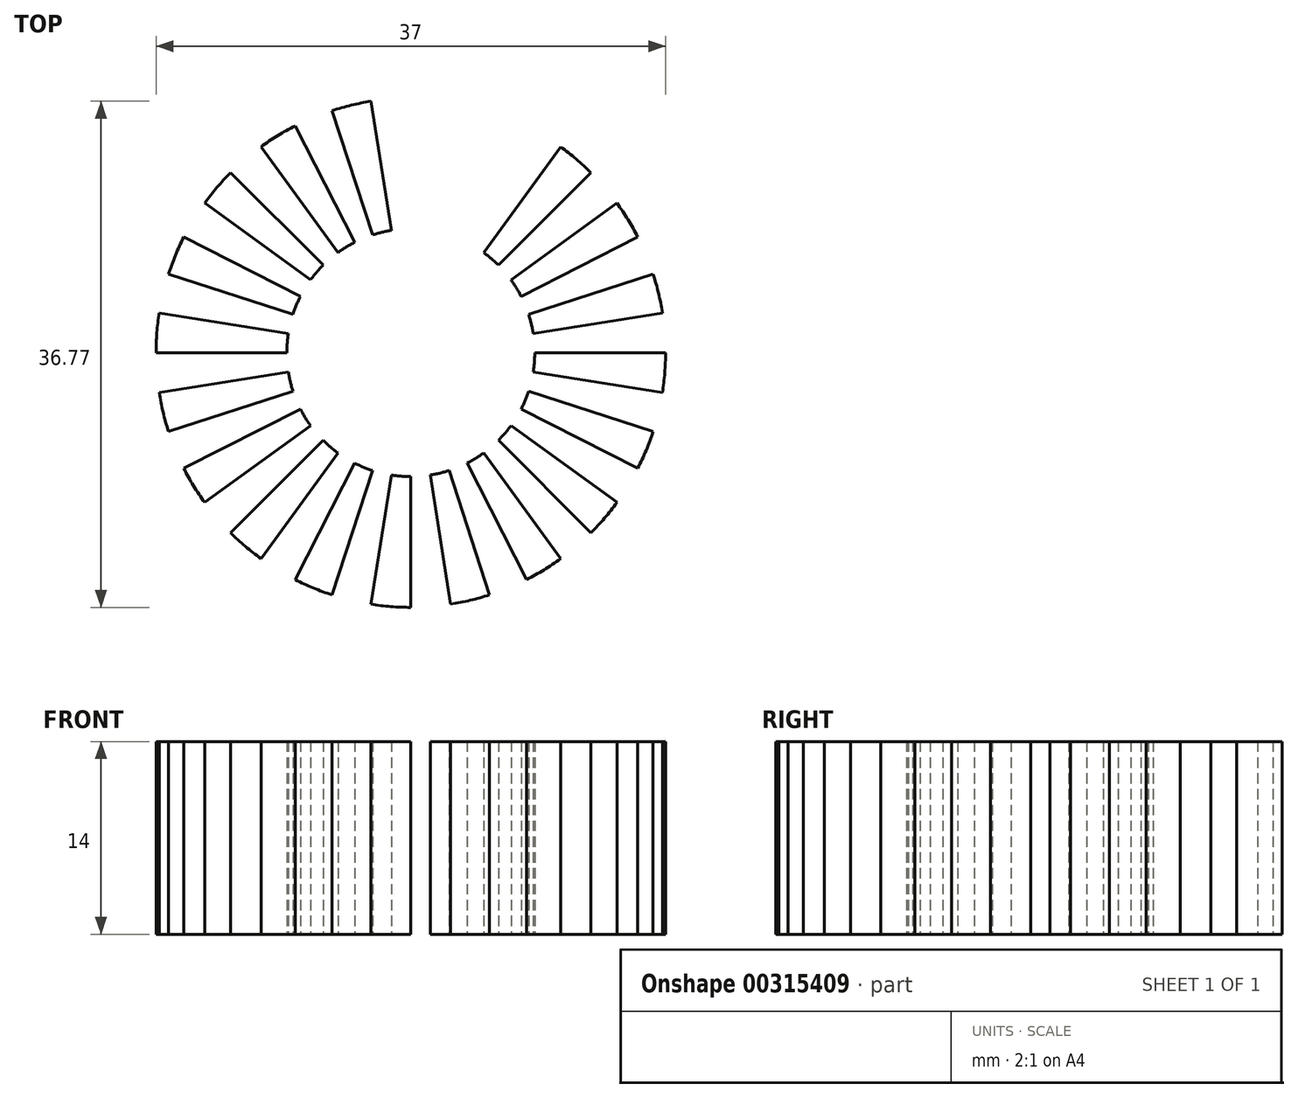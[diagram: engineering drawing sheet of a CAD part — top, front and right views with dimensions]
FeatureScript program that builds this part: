
annotation { "Feature Type Name" : "Feature", "Feature Type Description" : "" }
export const myFeature = defineFeature(function(context is Context, id is Id, definition is map)
    precondition{}
    {
        {
            var Q0;
            Q0=qCreatedBy(makeId("Top.planeOp"),FACE);
            var sketch = newSketch(context, id + "F0", { "sketchPlane" : qUnion([Q0])});
            skCircle(sketch, "E0", {"center": v(0, 0) * mm, "radius": 18.5 * mm, "construction": true});
            skArc(sketch, "E1", {"start": v(0, 18.5) * mm, "mid": v(1.45, 18.44) * mm, "end": v(2.9, 18.27) * mm});
            skLineSegment(sketch, "E2", {"start": v(2.9, 18.27) * mm, "end": v(1.4, 8.89) * mm});
            skArc(sketch, "E3", {"start": v(2.66, 16.8) * mm, "mid": v(3.97, 16.53) * mm, "end": v(5.25, 16.17) * mm});
            skLineSegment(sketch, "E4", {"start": v(5.25, 16.17) * mm, "end": v(2.78, 8.56) * mm});
            skLineSegment(sketch, "E5", {"start": v(0, 18.5) * mm, "end": v(0, 9) * mm});
            skArc(sketch, "E6", {"start": v(2.78, 8.56) * mm, "mid": v(1.4, 8.89) * mm, "end": v(0, 9) * mm});
            skLineSegment(sketch, "E7.1.0", {"start": v(-5.72, 17.6) * mm, "end": v(-2.78, 8.56) * mm});
            skArc(sketch, "E7.1.1", {"start": v(0, 9) * mm, "mid": v(-1.4, 8.89) * mm, "end": v(-2.78, 8.56) * mm});
            skLineSegment(sketch, "E7.1.2", {"start": v(0, 17) * mm, "end": v(0, 9) * mm});
            skArc(sketch, "E7.1.3", {"start": v(-2.66, 16.8) * mm, "mid": v(-1.33, 16.95) * mm, "end": v(0, 17) * mm});
            skLineSegment(sketch, "E7.1.4", {"start": v(-2.9, 18.27) * mm, "end": v(-1.4, 8.89) * mm});
            skArc(sketch, "E7.1.5", {"start": v(-5.72, 17.6) * mm, "mid": v(-4.32, 17.99) * mm, "end": v(-2.9, 18.27) * mm});
            skLineSegment(sketch, "E7.2.0", {"start": v(-10.87, 14.97) * mm, "end": v(-5.3, 7.28) * mm});
            skArc(sketch, "E7.2.1", {"start": v(-2.78, 8.56) * mm, "mid": v(-4.09, 8.02) * mm, "end": v(-5.3, 7.28) * mm});
            skLineSegment(sketch, "E7.2.2", {"start": v(-5.25, 16.17) * mm, "end": v(-2.78, 8.56) * mm});
            skArc(sketch, "E7.2.3", {"start": v(-7.72, 15.15) * mm, "mid": v(-6.5, 15.7) * mm, "end": v(-5.25, 16.17) * mm});
            skLineSegment(sketch, "E7.2.4", {"start": v(-8.4, 16.48) * mm, "end": v(-4.09, 8.02) * mm});
            skArc(sketch, "E7.2.5", {"start": v(-10.87, 14.97) * mm, "mid": v(-9.67, 15.77) * mm, "end": v(-8.4, 16.48) * mm});
            skLineSegment(sketch, "E7.3.0", {"start": v(-14.97, 10.87) * mm, "end": v(-7.28, 5.3) * mm});
            skArc(sketch, "E7.3.1", {"start": v(-5.3, 7.28) * mm, "mid": v(-6.36, 6.36) * mm, "end": v(-7.28, 5.3) * mm});
            skLineSegment(sketch, "E7.3.2", {"start": v(-10, 13.75) * mm, "end": v(-5.3, 7.28) * mm});
            skArc(sketch, "E7.3.3", {"start": v(-12.02, 12.02) * mm, "mid": v(-11.04, 12.93) * mm, "end": v(-10, 13.75) * mm});
            skLineSegment(sketch, "E7.3.4", {"start": v(-13.08, 13.08) * mm, "end": v(-6.36, 6.36) * mm});
            skArc(sketch, "E7.3.5", {"start": v(-14.97, 10.87) * mm, "mid": v(-14.07, 12.01) * mm, "end": v(-13.08, 13.08) * mm});
            skLineSegment(sketch, "E7.4.0", {"start": v(-17.6, 5.72) * mm, "end": v(-8.56, 2.78) * mm});
            skArc(sketch, "E7.4.1", {"start": v(-7.28, 5.3) * mm, "mid": v(-8.02, 4.09) * mm, "end": v(-8.56, 2.78) * mm});
            skLineSegment(sketch, "E7.4.2", {"start": v(-13.75, 10) * mm, "end": v(-7.28, 5.3) * mm});
            skArc(sketch, "E7.4.3", {"start": v(-15.15, 7.72) * mm, "mid": v(-14.5, 8.88) * mm, "end": v(-13.75, 10) * mm});
            skLineSegment(sketch, "E7.4.4", {"start": v(-16.48, 8.4) * mm, "end": v(-8.02, 4.09) * mm});
            skArc(sketch, "E7.4.5", {"start": v(-17.6, 5.72) * mm, "mid": v(-17.1, 7.08) * mm, "end": v(-16.48, 8.4) * mm});
            skLineSegment(sketch, "E7.5.0", {"start": v(-18.5, 0) * mm, "end": v(-9, 0) * mm});
            skArc(sketch, "E7.5.1", {"start": v(-8.56, 2.78) * mm, "mid": v(-8.89, 1.4) * mm, "end": v(-9, 0) * mm});
            skLineSegment(sketch, "E7.5.2", {"start": v(-16.17, 5.25) * mm, "end": v(-8.56, 2.78) * mm});
            skArc(sketch, "E7.5.3", {"start": v(-16.8, 2.66) * mm, "mid": v(-16.53, 3.97) * mm, "end": v(-16.17, 5.25) * mm});
            skLineSegment(sketch, "E7.5.4", {"start": v(-18.27, 2.9) * mm, "end": v(-8.89, 1.4) * mm});
            skArc(sketch, "E7.5.5", {"start": v(-18.5, 0) * mm, "mid": v(-18.44, 1.45) * mm, "end": v(-18.27, 2.9) * mm});
            skLineSegment(sketch, "E7.6.0", {"start": v(-17.6, -5.72) * mm, "end": v(-8.56, -2.78) * mm});
            skArc(sketch, "E7.6.1", {"start": v(-9, 0) * mm, "mid": v(-8.89, -1.4) * mm, "end": v(-8.56, -2.78) * mm});
            skLineSegment(sketch, "E7.6.2", {"start": v(-17, 0) * mm, "end": v(-9, 0) * mm});
            skArc(sketch, "E7.6.3", {"start": v(-16.8, -2.66) * mm, "mid": v(-16.95, -1.33) * mm, "end": v(-17, 0) * mm});
            skLineSegment(sketch, "E7.6.4", {"start": v(-18.27, -2.9) * mm, "end": v(-8.89, -1.4) * mm});
            skArc(sketch, "E7.6.5", {"start": v(-17.6, -5.72) * mm, "mid": v(-17.99, -4.32) * mm, "end": v(-18.27, -2.9) * mm});
            skLineSegment(sketch, "E7.7.0", {"start": v(-14.97, -10.87) * mm, "end": v(-7.28, -5.3) * mm});
            skArc(sketch, "E7.7.1", {"start": v(-8.56, -2.78) * mm, "mid": v(-8.02, -4.09) * mm, "end": v(-7.28, -5.3) * mm});
            skLineSegment(sketch, "E7.7.2", {"start": v(-16.17, -5.25) * mm, "end": v(-8.56, -2.78) * mm});
            skArc(sketch, "E7.7.3", {"start": v(-15.15, -7.72) * mm, "mid": v(-15.7, -6.5) * mm, "end": v(-16.17, -5.25) * mm});
            skLineSegment(sketch, "E7.7.4", {"start": v(-16.48, -8.4) * mm, "end": v(-8.02, -4.09) * mm});
            skArc(sketch, "E7.7.5", {"start": v(-14.97, -10.87) * mm, "mid": v(-15.77, -9.67) * mm, "end": v(-16.48, -8.4) * mm});
            skLineSegment(sketch, "E7.8.0", {"start": v(-10.87, -14.97) * mm, "end": v(-5.3, -7.28) * mm});
            skArc(sketch, "E7.8.1", {"start": v(-7.28, -5.3) * mm, "mid": v(-6.36, -6.36) * mm, "end": v(-5.3, -7.28) * mm});
            skLineSegment(sketch, "E7.8.2", {"start": v(-13.75, -10) * mm, "end": v(-7.28, -5.3) * mm});
            skArc(sketch, "E7.8.3", {"start": v(-12.02, -12.02) * mm, "mid": v(-12.93, -11.04) * mm, "end": v(-13.75, -10) * mm});
            skLineSegment(sketch, "E7.8.4", {"start": v(-13.08, -13.08) * mm, "end": v(-6.36, -6.36) * mm});
            skArc(sketch, "E7.8.5", {"start": v(-10.87, -14.97) * mm, "mid": v(-12.01, -14.07) * mm, "end": v(-13.08, -13.08) * mm});
            skLineSegment(sketch, "E7.9.0", {"start": v(-5.72, -17.6) * mm, "end": v(-2.78, -8.56) * mm});
            skArc(sketch, "E7.9.1", {"start": v(-5.3, -7.28) * mm, "mid": v(-4.09, -8.02) * mm, "end": v(-2.78, -8.56) * mm});
            skLineSegment(sketch, "E7.9.2", {"start": v(-10, -13.75) * mm, "end": v(-5.3, -7.28) * mm});
            skArc(sketch, "E7.9.3", {"start": v(-7.72, -15.15) * mm, "mid": v(-8.88, -14.5) * mm, "end": v(-10, -13.75) * mm});
            skLineSegment(sketch, "E7.9.4", {"start": v(-8.4, -16.48) * mm, "end": v(-4.09, -8.02) * mm});
            skArc(sketch, "E7.9.5", {"start": v(-5.72, -17.6) * mm, "mid": v(-7.08, -17.1) * mm, "end": v(-8.4, -16.48) * mm});
            skLineSegment(sketch, "E7.10.0", {"start": v(0, -18.5) * mm, "end": v(0, -9) * mm});
            skArc(sketch, "E7.10.1", {"start": v(-2.78, -8.56) * mm, "mid": v(-1.4, -8.89) * mm, "end": v(0, -9) * mm});
            skLineSegment(sketch, "E7.10.2", {"start": v(-5.25, -16.17) * mm, "end": v(-2.78, -8.56) * mm});
            skArc(sketch, "E7.10.3", {"start": v(-2.66, -16.8) * mm, "mid": v(-3.97, -16.53) * mm, "end": v(-5.25, -16.17) * mm});
            skLineSegment(sketch, "E7.10.4", {"start": v(-2.9, -18.27) * mm, "end": v(-1.4, -8.89) * mm});
            skArc(sketch, "E7.10.5", {"start": v(0, -18.5) * mm, "mid": v(-1.45, -18.44) * mm, "end": v(-2.9, -18.27) * mm});
            skLineSegment(sketch, "E7.11.0", {"start": v(5.72, -17.6) * mm, "end": v(2.78, -8.56) * mm});
            skArc(sketch, "E7.11.1", {"start": v(0, -9) * mm, "mid": v(1.4, -8.89) * mm, "end": v(2.78, -8.56) * mm});
            skLineSegment(sketch, "E7.11.2", {"start": v(0, -17) * mm, "end": v(0, -9) * mm});
            skArc(sketch, "E7.11.3", {"start": v(2.66, -16.8) * mm, "mid": v(1.33, -16.95) * mm, "end": v(0, -17) * mm});
            skLineSegment(sketch, "E7.11.4", {"start": v(2.9, -18.27) * mm, "end": v(1.4, -8.89) * mm});
            skArc(sketch, "E7.11.5", {"start": v(5.72, -17.6) * mm, "mid": v(4.32, -17.99) * mm, "end": v(2.9, -18.27) * mm});
            skLineSegment(sketch, "E7.12.0", {"start": v(10.87, -14.97) * mm, "end": v(5.3, -7.28) * mm});
            skArc(sketch, "E7.12.1", {"start": v(2.78, -8.56) * mm, "mid": v(4.09, -8.02) * mm, "end": v(5.3, -7.28) * mm});
            skLineSegment(sketch, "E7.12.2", {"start": v(5.25, -16.17) * mm, "end": v(2.78, -8.56) * mm});
            skArc(sketch, "E7.12.3", {"start": v(7.72, -15.15) * mm, "mid": v(6.5, -15.7) * mm, "end": v(5.25, -16.17) * mm});
            skLineSegment(sketch, "E7.12.4", {"start": v(8.4, -16.48) * mm, "end": v(4.09, -8.02) * mm});
            skArc(sketch, "E7.12.5", {"start": v(10.87, -14.97) * mm, "mid": v(9.67, -15.77) * mm, "end": v(8.4, -16.48) * mm});
            skLineSegment(sketch, "E7.13.0", {"start": v(14.97, -10.87) * mm, "end": v(7.28, -5.3) * mm});
            skArc(sketch, "E7.13.1", {"start": v(5.3, -7.28) * mm, "mid": v(6.36, -6.36) * mm, "end": v(7.28, -5.3) * mm});
            skLineSegment(sketch, "E7.13.2", {"start": v(10, -13.75) * mm, "end": v(5.3, -7.28) * mm});
            skArc(sketch, "E7.13.3", {"start": v(12.02, -12.02) * mm, "mid": v(11.04, -12.93) * mm, "end": v(10, -13.75) * mm});
            skLineSegment(sketch, "E7.13.4", {"start": v(13.08, -13.08) * mm, "end": v(6.36, -6.36) * mm});
            skArc(sketch, "E7.13.5", {"start": v(14.97, -10.87) * mm, "mid": v(14.07, -12.01) * mm, "end": v(13.08, -13.08) * mm});
            skLineSegment(sketch, "E7.14.0", {"start": v(17.6, -5.72) * mm, "end": v(8.56, -2.78) * mm});
            skArc(sketch, "E7.14.1", {"start": v(7.28, -5.3) * mm, "mid": v(8.02, -4.09) * mm, "end": v(8.56, -2.78) * mm});
            skLineSegment(sketch, "E7.14.2", {"start": v(13.75, -10) * mm, "end": v(7.28, -5.3) * mm});
            skArc(sketch, "E7.14.3", {"start": v(15.15, -7.72) * mm, "mid": v(14.5, -8.88) * mm, "end": v(13.75, -10) * mm});
            skLineSegment(sketch, "E7.14.4", {"start": v(16.48, -8.4) * mm, "end": v(8.02, -4.09) * mm});
            skArc(sketch, "E7.14.5", {"start": v(17.6, -5.72) * mm, "mid": v(17.1, -7.08) * mm, "end": v(16.48, -8.4) * mm});
            skLineSegment(sketch, "E7.15.0", {"start": v(18.5, 0) * mm, "end": v(9, 0) * mm});
            skArc(sketch, "E7.15.1", {"start": v(8.56, -2.78) * mm, "mid": v(8.89, -1.4) * mm, "end": v(9, 0) * mm});
            skLineSegment(sketch, "E7.15.2", {"start": v(16.17, -5.25) * mm, "end": v(8.56, -2.78) * mm});
            skArc(sketch, "E7.15.3", {"start": v(16.8, -2.66) * mm, "mid": v(16.53, -3.97) * mm, "end": v(16.17, -5.25) * mm});
            skLineSegment(sketch, "E7.15.4", {"start": v(18.27, -2.9) * mm, "end": v(8.89, -1.4) * mm});
            skArc(sketch, "E7.15.5", {"start": v(18.5, 0) * mm, "mid": v(18.44, -1.45) * mm, "end": v(18.27, -2.9) * mm});
            skLineSegment(sketch, "E7.16.0", {"start": v(17.6, 5.72) * mm, "end": v(8.56, 2.78) * mm});
            skArc(sketch, "E7.16.1", {"start": v(9, 0) * mm, "mid": v(8.89, 1.4) * mm, "end": v(8.56, 2.78) * mm});
            skLineSegment(sketch, "E7.16.2", {"start": v(17, 0) * mm, "end": v(9, 0) * mm});
            skArc(sketch, "E7.16.3", {"start": v(16.8, 2.66) * mm, "mid": v(16.95, 1.33) * mm, "end": v(17, 0) * mm});
            skLineSegment(sketch, "E7.16.4", {"start": v(18.27, 2.9) * mm, "end": v(8.89, 1.4) * mm});
            skArc(sketch, "E7.16.5", {"start": v(17.6, 5.72) * mm, "mid": v(17.99, 4.32) * mm, "end": v(18.27, 2.9) * mm});
            skLineSegment(sketch, "E7.17.0", {"start": v(14.97, 10.87) * mm, "end": v(7.28, 5.3) * mm});
            skArc(sketch, "E7.17.1", {"start": v(8.56, 2.78) * mm, "mid": v(8.02, 4.09) * mm, "end": v(7.28, 5.3) * mm});
            skLineSegment(sketch, "E7.17.2", {"start": v(16.17, 5.25) * mm, "end": v(8.56, 2.78) * mm});
            skArc(sketch, "E7.17.3", {"start": v(15.15, 7.72) * mm, "mid": v(15.7, 6.5) * mm, "end": v(16.17, 5.25) * mm});
            skLineSegment(sketch, "E7.17.4", {"start": v(16.48, 8.4) * mm, "end": v(8.02, 4.09) * mm});
            skArc(sketch, "E7.17.5", {"start": v(14.97, 10.87) * mm, "mid": v(15.77, 9.67) * mm, "end": v(16.48, 8.4) * mm});
            skLineSegment(sketch, "E7.18.0", {"start": v(10.87, 14.97) * mm, "end": v(5.3, 7.28) * mm});
            skArc(sketch, "E7.18.1", {"start": v(7.28, 5.3) * mm, "mid": v(6.36, 6.36) * mm, "end": v(5.3, 7.28) * mm});
            skLineSegment(sketch, "E7.18.2", {"start": v(13.75, 10) * mm, "end": v(7.28, 5.3) * mm});
            skArc(sketch, "E7.18.3", {"start": v(12.02, 12.02) * mm, "mid": v(12.93, 11.04) * mm, "end": v(13.75, 10) * mm});
            skLineSegment(sketch, "E7.18.4", {"start": v(13.08, 13.08) * mm, "end": v(6.36, 6.36) * mm});
            skArc(sketch, "E7.18.5", {"start": v(10.87, 14.97) * mm, "mid": v(12.01, 14.07) * mm, "end": v(13.08, 13.08) * mm});
            skLineSegment(sketch, "E7.19.0", {"start": v(5.72, 17.6) * mm, "end": v(2.78, 8.56) * mm});
            skArc(sketch, "E7.19.1", {"start": v(5.3, 7.28) * mm, "mid": v(4.09, 8.02) * mm, "end": v(2.78, 8.56) * mm});
            skLineSegment(sketch, "E7.19.2", {"start": v(10, 13.75) * mm, "end": v(5.3, 7.28) * mm});
            skArc(sketch, "E7.19.3", {"start": v(7.72, 15.15) * mm, "mid": v(8.88, 14.5) * mm, "end": v(10, 13.75) * mm});
            skLineSegment(sketch, "E7.19.4", {"start": v(8.4, 16.48) * mm, "end": v(4.09, 8.02) * mm});
            skArc(sketch, "E7.19.5", {"start": v(5.72, 17.6) * mm, "mid": v(7.08, 17.1) * mm, "end": v(8.4, 16.48) * mm});
            skSolve(sketch);
        }
        {
            var Q0;
            Q0=makeQuery(id+"F0.imprint","IMPRINT",FACE,{"disambiguationData":[TD([[makeQuery(id+"F0.imprint","IMPRINT",EDGE,{"derivedFrom":sQuery(id+"F0.wireOp",EDGE,"E7.13.0")}),1.0]])]});
            var Q1;
            {var subQ0=sQuery(id+"F0.wireOp",EDGE,"E7.14.2");Q1=makeQuery(id+"F0.imprint","IMPRINT",FACE,{"disambiguationData":[TD([[makeQuery(id+"F0.imprint","IMPRINT",EDGE,{"derivedFrom":subQ0}),-1.0]])]});}
            var Q2;
            {var subQ0=sQuery(id+"F0.wireOp",EDGE,"E7.13.2");Q2=makeQuery(id+"F0.imprint","IMPRINT",FACE,{"disambiguationData":[TD([[makeQuery(id+"F0.imprint","IMPRINT",EDGE,{"derivedFrom":subQ0}),-1.0]])]});}
            var Q3;
            Q3=makeQuery(id+"F0.imprint","IMPRINT",FACE,{"disambiguationData":[TD([[makeQuery(id+"F0.imprint","IMPRINT",EDGE,{"derivedFrom":sQuery(id+"F0.wireOp",EDGE,"E7.15.0")}),1.0]])]});
            var Q4;
            Q4=makeQuery(id+"F0.imprint","IMPRINT",FACE,{"disambiguationData":[TD([[makeQuery(id+"F0.imprint","IMPRINT",EDGE,{"derivedFrom":sQuery(id+"F0.wireOp",EDGE,"E7.14.0")}),1.0]])]});
            var Q5;
            Q5=makeQuery(id+"F0.imprint","IMPRINT",FACE,{"disambiguationData":[TD([[makeQuery(id+"F0.imprint","IMPRINT",EDGE,{"derivedFrom":sQuery(id+"F0.wireOp",EDGE,"E7.8.0")}),1.0]])]});
            var Q6;
            Q6=makeQuery(id+"F0.imprint","IMPRINT",FACE,{"disambiguationData":[TD([[makeQuery(id+"F0.imprint","IMPRINT",EDGE,{"derivedFrom":sQuery(id+"F0.wireOp",EDGE,"E7.16.0")}),1.0]])]});
            var Q7;
            {var subQ0=sQuery(id+"F0.wireOp",EDGE,"E7.8.2");Q7=makeQuery(id+"F0.imprint","IMPRINT",FACE,{"disambiguationData":[TD([[makeQuery(id+"F0.imprint","IMPRINT",EDGE,{"derivedFrom":subQ0}),-1.0]])]});}
            var Q8;
            {var subQ0=sQuery(id+"F0.wireOp",EDGE,"E7.16.2");Q8=makeQuery(id+"F0.imprint","IMPRINT",FACE,{"disambiguationData":[TD([[makeQuery(id+"F0.imprint","IMPRINT",EDGE,{"derivedFrom":subQ0}),-1.0]])]});}
            var Q9;
            Q9=makeQuery(id+"F0.imprint","IMPRINT",FACE,{"disambiguationData":[TD([[makeQuery(id+"F0.imprint","IMPRINT",EDGE,{"derivedFrom":sQuery(id+"F0.wireOp",EDGE,"E7.9.0")}),1.0]])]});
            var Q10;
            Q10=makeQuery(id+"F0.imprint","IMPRINT",FACE,{"disambiguationData":[TD([[makeQuery(id+"F0.imprint","IMPRINT",EDGE,{"derivedFrom":sQuery(id+"F0.wireOp",EDGE,"E7.17.0")}),1.0]])]});
            var Q11;
            {var subQ0=sQuery(id+"F0.wireOp",EDGE,"E7.9.2");Q11=makeQuery(id+"F0.imprint","IMPRINT",FACE,{"disambiguationData":[TD([[makeQuery(id+"F0.imprint","IMPRINT",EDGE,{"derivedFrom":subQ0}),-1.0]])]});}
            var Q12;
            {var subQ0=sQuery(id+"F0.wireOp",EDGE,"E7.17.2");Q12=makeQuery(id+"F0.imprint","IMPRINT",FACE,{"disambiguationData":[TD([[makeQuery(id+"F0.imprint","IMPRINT",EDGE,{"derivedFrom":subQ0}),-1.0]])]});}
            var Q13;
            Q13=makeQuery(id+"F0.imprint","IMPRINT",FACE,{"disambiguationData":[TD([[makeQuery(id+"F0.imprint","IMPRINT",EDGE,{"derivedFrom":sQuery(id+"F0.wireOp",EDGE,"E7.10.0")}),1.0]])]});
            var Q14;
            Q14=makeQuery(id+"F0.imprint","IMPRINT",FACE,{"disambiguationData":[TD([[makeQuery(id+"F0.imprint","IMPRINT",EDGE,{"derivedFrom":sQuery(id+"F0.wireOp",EDGE,"E7.18.0")}),1.0]])]});
            var Q15;
            {var subQ0=sQuery(id+"F0.wireOp",EDGE,"E7.10.2");Q15=makeQuery(id+"F0.imprint","IMPRINT",FACE,{"disambiguationData":[TD([[makeQuery(id+"F0.imprint","IMPRINT",EDGE,{"derivedFrom":subQ0}),-1.0]])]});}
            var Q16;
            {var subQ0=sQuery(id+"F0.wireOp",EDGE,"E7.18.2");Q16=makeQuery(id+"F0.imprint","IMPRINT",FACE,{"disambiguationData":[TD([[makeQuery(id+"F0.imprint","IMPRINT",EDGE,{"derivedFrom":subQ0}),-1.0]])]});}
            var Q17;
            {var subQ6=sQuery(id+"F0.wireOp",EDGE,"E7.19.5");Q17=makeQuery(id+"F0.imprint","IMPRINT",FACE,{"disambiguationData":[TD([[makeQuery(id+"F0.imprint","IMPRINT",EDGE,{"derivedFrom":subQ6}),-1.0]])]});}
            var Q18;
            Q18=makeQuery(id+"F0.imprint","IMPRINT",FACE,{"disambiguationData":[TD([[makeQuery(id+"F0.imprint","IMPRINT",EDGE,{"derivedFrom":sQuery(id+"F0.wireOp",EDGE,"E7.11.0")}),1.0]])]});
            var Q19;
            {var subQ0=sQuery(id+"F0.wireOp",EDGE,"E7.7.2");Q19=makeQuery(id+"F0.imprint","IMPRINT",FACE,{"disambiguationData":[TD([[makeQuery(id+"F0.imprint","IMPRINT",EDGE,{"derivedFrom":subQ0}),-1.0]])]});}
            var Q20;
            {var subQ0=sQuery(id+"F0.wireOp",EDGE,"E7.6.2");Q20=makeQuery(id+"F0.imprint","IMPRINT",FACE,{"disambiguationData":[TD([[makeQuery(id+"F0.imprint","IMPRINT",EDGE,{"derivedFrom":subQ0}),-1.0]])]});}
            var Q21;
            Q21=makeQuery(id+"F0.imprint","IMPRINT",FACE,{"disambiguationData":[TD([[makeQuery(id+"F0.imprint","IMPRINT",EDGE,{"derivedFrom":sQuery(id+"F0.wireOp",EDGE,"E7.7.0")}),1.0]])]});
            var Q22;
            {var subQ4=sQuery(id+"F0.wireOp",EDGE,"E1");Q22=makeQuery(id+"F0.imprint","IMPRINT",FACE,{"disambiguationData":[TD([[makeQuery(id+"F0.imprint","IMPRINT",EDGE,{"derivedFrom":subQ4}),-1.0]])]});}
            var Q23;
            {var subQ3=sQuery(id+"F0.wireOp",EDGE,"E3");Q23=makeQuery(id+"F0.imprint","IMPRINT",FACE,{"disambiguationData":[TD([[makeQuery(id+"F0.imprint","IMPRINT",EDGE,{"derivedFrom":subQ3}),-1.0]])]});}
            var Q24;
            Q24=makeQuery(id+"F0.imprint","IMPRINT",FACE,{"disambiguationData":[TD([[makeQuery(id+"F0.imprint","IMPRINT",EDGE,{"derivedFrom":sQuery(id+"F0.wireOp",EDGE,"E7.1.0")}),1.0]])]});
            var Q25;
            {var subQ0=sQuery(id+"F0.wireOp",EDGE,"E7.1.2");Q25=makeQuery(id+"F0.imprint","IMPRINT",FACE,{"disambiguationData":[TD([[makeQuery(id+"F0.imprint","IMPRINT",EDGE,{"derivedFrom":subQ0}),-1.0]])]});}
            var Q26;
            Q26=makeQuery(id+"F0.imprint","IMPRINT",FACE,{"disambiguationData":[TD([[makeQuery(id+"F0.imprint","IMPRINT",EDGE,{"derivedFrom":sQuery(id+"F0.wireOp",EDGE,"E7.2.0")}),1.0]])]});
            var Q27;
            {var subQ0=sQuery(id+"F0.wireOp",EDGE,"E7.2.2");Q27=makeQuery(id+"F0.imprint","IMPRINT",FACE,{"disambiguationData":[TD([[makeQuery(id+"F0.imprint","IMPRINT",EDGE,{"derivedFrom":subQ0}),-1.0]])]});}
            var Q28;
            Q28=makeQuery(id+"F0.imprint","IMPRINT",FACE,{"disambiguationData":[TD([[makeQuery(id+"F0.imprint","IMPRINT",EDGE,{"derivedFrom":sQuery(id+"F0.wireOp",EDGE,"E7.3.0")}),1.0]])]});
            var Q29;
            {var subQ0=sQuery(id+"F0.wireOp",EDGE,"E7.3.2");Q29=makeQuery(id+"F0.imprint","IMPRINT",FACE,{"disambiguationData":[TD([[makeQuery(id+"F0.imprint","IMPRINT",EDGE,{"derivedFrom":subQ0}),-1.0]])]});}
            var Q30;
            Q30=makeQuery(id+"F0.imprint","IMPRINT",FACE,{"disambiguationData":[TD([[makeQuery(id+"F0.imprint","IMPRINT",EDGE,{"derivedFrom":sQuery(id+"F0.wireOp",EDGE,"E7.4.0")}),1.0]])]});
            var Q31;
            {var subQ0=sQuery(id+"F0.wireOp",EDGE,"E7.4.2");Q31=makeQuery(id+"F0.imprint","IMPRINT",FACE,{"disambiguationData":[TD([[makeQuery(id+"F0.imprint","IMPRINT",EDGE,{"derivedFrom":subQ0}),-1.0]])]});}
            var Q32;
            Q32=makeQuery(id+"F0.imprint","IMPRINT",FACE,{"disambiguationData":[TD([[makeQuery(id+"F0.imprint","IMPRINT",EDGE,{"derivedFrom":sQuery(id+"F0.wireOp",EDGE,"E7.5.0")}),1.0]])]});
            var Q33;
            {var subQ0=sQuery(id+"F0.wireOp",EDGE,"E7.5.2");Q33=makeQuery(id+"F0.imprint","IMPRINT",FACE,{"disambiguationData":[TD([[makeQuery(id+"F0.imprint","IMPRINT",EDGE,{"derivedFrom":subQ0}),-1.0]])]});}
            var Q34;
            Q34=makeQuery(id+"F0.imprint","IMPRINT",FACE,{"disambiguationData":[TD([[makeQuery(id+"F0.imprint","IMPRINT",EDGE,{"derivedFrom":sQuery(id+"F0.wireOp",EDGE,"E7.6.0")}),1.0]])]});
            var Q35;
            {var subQ0=sQuery(id+"F0.wireOp",EDGE,"E7.19.2");Q35=makeQuery(id+"F0.imprint","IMPRINT",FACE,{"disambiguationData":[TD([[makeQuery(id+"F0.imprint","IMPRINT",EDGE,{"derivedFrom":subQ0}),-1.0]])]});}
            var Q36;
            {var subQ0=sQuery(id+"F0.wireOp",EDGE,"E7.11.2");Q36=makeQuery(id+"F0.imprint","IMPRINT",FACE,{"disambiguationData":[TD([[makeQuery(id+"F0.imprint","IMPRINT",EDGE,{"derivedFrom":subQ0}),-1.0]])]});}
            var Q37;
            Q37=makeQuery(id+"F0.imprint","IMPRINT",FACE,{"disambiguationData":[TD([[makeQuery(id+"F0.imprint","IMPRINT",EDGE,{"derivedFrom":sQuery(id+"F0.wireOp",EDGE,"E7.12.0")}),1.0]])]});
            var Q38;
            {var subQ0=sQuery(id+"F0.wireOp",EDGE,"E7.15.2");Q38=makeQuery(id+"F0.imprint","IMPRINT",FACE,{"disambiguationData":[TD([[makeQuery(id+"F0.imprint","IMPRINT",EDGE,{"derivedFrom":subQ0}),-1.0]])]});}
            var Q39;
            {var subQ0=sQuery(id+"F0.wireOp",EDGE,"E7.12.2");Q39=makeQuery(id+"F0.imprint","IMPRINT",FACE,{"disambiguationData":[TD([[makeQuery(id+"F0.imprint","IMPRINT",EDGE,{"derivedFrom":subQ0}),-1.0]])]});}
            extrude(context, id + "F1", {"entities" : qUnion([Q0, Q1, Q2, Q3, Q4, Q5, Q6, Q7, Q8, Q9, Q10, Q11, Q12, Q13, Q14, Q15, Q16, Q17, Q18, Q19, Q20, Q21, Q22, Q23, Q24, Q25, Q26, Q27, Q28, Q29, Q30, Q31, Q32, Q33, Q34, Q35, Q36, Q37, Q38, Q39]), "depth" : 14 * mm});
        }
    });
